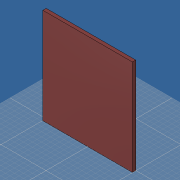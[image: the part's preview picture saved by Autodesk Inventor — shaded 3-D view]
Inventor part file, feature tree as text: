
AUTODESK INVENTOR PART (.ipt)
format: ipt  version: 2019 (Build 230136000, 136)  size: 96,256 bytes
history: native  units: mm
features: extrude x2, other x1, sketch x1
ambient origin geometry x8: Origin, YZ Plane, XZ Plane, XY Plane, X Axis, Y Axis, Z Axis, Center Point
bodies: Volumenkörper1 (feature_tree)
feature tree (4):
  other  "<userpath>\OneDrive\Dokumente\Inventor\Absauganlage\Absauganlage_Params.xlsx"
  sketch  "Skizze1"  dims[d0=398.0mm d1=425.0mm d2=15.0mm d3=0.0mm d5=17.0mm d6=6.0mm d7=0.0mm d8=17.0mm d9=17.0mm d10=8.0mm]
  extrude  "Extrusion1"  Depth=425.0mm
  extrude  "Extrusion2"  Depth=15.0mm
